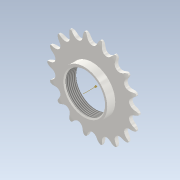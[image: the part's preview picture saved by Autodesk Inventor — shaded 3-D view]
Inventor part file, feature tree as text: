
AUTODESK INVENTOR PART (.ipt)
format: ipt  version: 2021 (Build 250183000, 183)  size: 480,256 bytes
history: native  units: mm
features: other x7, extrude x3, pattern_linear x1, pattern_circular x1, hole x1, chamfer x1, sketch x1
ambient origin geometry x8: Origin, YZ Plane, XZ Plane, XY Plane, X Axis, Y Axis, Z Axis, Center Point
bodies: Solid1 (feature_tree)
feature tree (15):
  other  "Theoretical Tooth Profile"
  other  "Tooth Profile"
  other  "Section Profile"
  other  "Shroud"
  other  "Strand"
  pattern_linear  "Strand Pattern"  Spacing1=3.490659mm  [1 undecoded]
  extrude  "Theoretical Tooth"  Depth=10.0mm
  extrude  "Tooth"  Depth=10.0mm
  pattern_circular  "Tooth Pattern"  [2 undecoded]
  other  "Timing Plane"
  other  "Punto de trabajo1"
  extrude  "Extrusión4"  Depth=10.0mm
  hole  "Agujero1"  [1 undecoded]
  chamfer  "Chaflán1"  Distance=10.85mm
  sketch  "Boceto4"  dims[d0=73.136385mm d2=3.490659mm d3=3.91375mm d10=22.398392mm d11=2.598601mm d12=6.2mm d13=10.11375mm d14=10.85mm d18=10.0mm d19=0.0mm d20=180.0mm d21=360.0deg d23=3.81mm d28=0.0mm d29=0.0mm d30=3.069mm d31=53.102879mm d32=3.069mm d33=0.762mm d34=12.7mm d36=90.0deg d37=90.0deg d38=10.0mm d40=13.92mm d42=0.0mm d43=1.5345mm d44=23.561945mm d45=18.6mm d46=3.91375mm d47=10.0mm d48=0.0mm d49=0.0mm d50=10.0mm d51=10.0mm d52=10.0mm d53=34.376202mm d54=72.0mm d55=66.51mm d56=23.55mm d57=90.0deg d58=8.0mm d59=20.594885mm d60=40.0mm d61=7.0mm d62=0.0mm d63=1.0mm d64=2.0mm d65=45.0deg]
note: 4 required parameter values undecoded (feature->parameter linkage not recoverable at this tier; creation-order binding heuristic only, values carry confidence <= 0.55)
